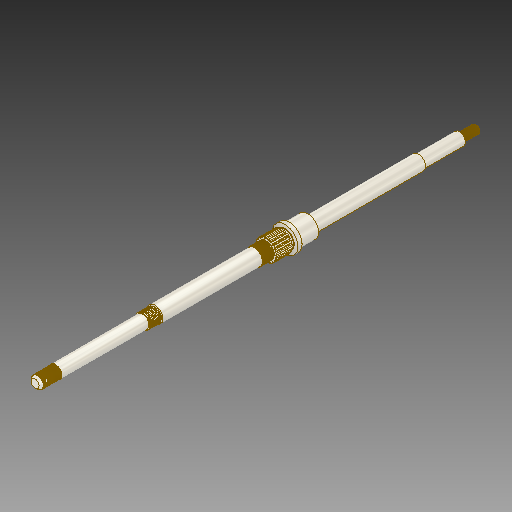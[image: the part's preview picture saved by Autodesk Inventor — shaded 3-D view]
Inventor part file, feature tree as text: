
AUTODESK INVENTOR PART (.ipt)
format: ipt  version: 2019 (Build 230136000, 136)  size: 991,232 bytes
history: native  units: mm
features: sketch x24, extrude x18, projected_geometry x7, helix x4, plane x3, split x2, fillet x2, hole x1, chamfer x1, other x1, revolve x1
ambient origin geometry x8: Origin, YZ Plane, XZ Plane, XY Plane, X Axis, Y Axis, Z Axis, Center Point
bodies: Solid1 (feature_tree)
feature tree (64):
  extrude  "Extrusion1"  Depth=23.0mm TaperAngle=0.0deg
  helix  "Coil1"  [1 undecoded]
  split  "Split1"
  extrude  "Extrusion2"  Depth=0.5mm
  extrude  "Extrusion16"  Depth=0.5mm
  extrude  "Extrusion3"  Depth=1.5mm
  extrude  "Extrusion4"  Depth=160.0mm TaperAngle=0.0deg
  extrude  "Extrusion5"  Depth=25.841mm TaperAngle=0.0deg
  extrude  "Extrusion6"  Depth=6.0mm TaperAngle=0.0deg
  extrude  "Extrusion7"  Depth=4.0mm TaperAngle=0.0deg
  extrude  "Extrusion8"  Depth=1.0mm
  extrude  "Extrusion9"  Depth=13.0mm
  helix  "Coil2"  [1 undecoded]
  extrude  "Extrusion10"  Depth=22.0mm TaperAngle=0.0deg
  plane  "Work Plane1"
  extrude  "Extrusion11"  Depth=155.0mm TaperAngle=0.0deg
  extrude  "Extrusion12"  TaperAngle=60.0deg  [1 undecoded]
  helix  "Coil3"  [1 undecoded]
  extrude  "Extrusion13"  Depth=0.5mm
  plane  "Work Plane2"
  extrude  "Extrusion14"  Depth=25.0mm
  extrude  "Extrusion15"  Depth=25.0mm
  helix  "Coil4"  [1 undecoded]
  split  "Split2"
  plane  "Work Plane3"
  hole  "Hole1"  [1 undecoded]
  fillet  "Fillet1"  Radius=1.241mm
  chamfer  "Chamfer1"  Distance=1.3mm
  fillet  "Fillet2"  [1 undecoded]
  extrude  "Extrusion17"  Depth=1.3mm TaperAngle=0.0deg
  extrude  "Extrusion18"  Depth=1.5mm TaperAngle=0.0deg
  sketch  "Sketch1"  dims[d0=10.5mm d1=23.0mm d2=0.0mm d7=0.747mm]
  sketch  "Sketch2"  dims[d9=60.0deg d10=0.5mm]
  sketch  "Sketch3"  dims[d12=60.0deg]
  sketch  "Sketch4"  dims[d14=1.0mm d15=0.5mm d16=230.0mm d17=0.0mm d18=90.0deg d19=90.0deg d20=0.0mm d21=0.0mm d22=12.0mm]
  sketch  "Sketch5"  dims[d23=1.5mm d24=0.0mm d25=20.0mm]
  sketch  "Sketch6"  dims[d26=154.0mm d27=0.0mm d29=160.0mm d30=0.0mm]
  sketch  "Sketch7"  dims[d31=30.0mm d32=25.841mm d33=0.0mm]
  sketch  "Sketch8"  dims[d34=36.0mm d35=6.0mm d36=0.0mm]
  sketch  "Sketch9"  dims[d37=25.0mm d38=4.0mm d39=0.0mm]
  sketch  "Sketch10"  dims[d40=29.0mm d41=1.0mm]
  sketch  "Sketch11"  dims[d42=13.0mm d43=19.896753mm d44=19.896753mm]
  projected_geometry  "Projected Loop2"
  sketch  "Sketch12"  dims[d45=220.0mm d47=360.0deg d49=22.0mm d50=0.0mm]
  sketch  "Sketch13"  dims[d51=22.0mm d52=155.0mm d53=0.0mm]
  projected_geometry  "Projected Loop3"
  sketch  "Sketch14"  dims[d54=0.717mm d56=60.0deg d57=0.45mm]
  sketch  "Sketch15"  dims[d58=1.0mm d59=0.5mm d60=230.0mm d61=0.0mm d62=90.0deg d63=90.0deg d64=0.0mm d65=0.0mm d66=21.4mm]
  projected_geometry  "Projected Loop4"
  sketch  "Sketch16"  dims[d67=1.7mm d68=0.0mm d69=25.0mm]
  sketch  "Sketch17"  dims[d70=-14.7mm d71=25.0mm d72=1.7mm d73=0.0mm]
  projected_geometry  "Projected Loop5"
  sketch  "Sketch18"  dims[d74=18.0mm d75=138.737mm d76=0.0mm d77=1.241mm]
  sketch  "Sketch19"  dims[d79=60.0deg]
  projected_geometry  "Projected Loop6"
  sketch  "Sketch20"  dims[d80=0.95mm]
  projected_geometry  "Projected Loop7"
  other  "Srf1"
  sketch  "Sketch21"  dims[d82=1.096966mm]
  sketch  "Sketch22"  dims[d83=1.5mm d84=10.0mm d85=200.0mm d86=0.0mm d87=90.0deg d88=90.0deg d89=0.0mm d90=0.0mm d91=1.3mm d92=0.0mm d93=-16.0mm]
  sketch  "Sketch23"  dims[d94=22.0mm d95=1.3mm d96=0.0mm]
  projected_geometry  "Projected Loop8"
  sketch  "Sketch24"  dims[d97=16.0mm d98=28.5mm d99=0.0mm d104=0.746mm d105=60.0deg d107=0.5mm d108=0.57735mm d109=1.0mm d110=10.0mm d111=300.0mm d112=0.0mm d113=90.0deg d114=90.0deg d115=0.0mm d116=0.0mm d117=6.859144mm d118=11.332mm d121=90.0deg d122=19.617501mm d123=8.25mm d124=3.5mm d125=6.0mm d126=4.0mm d127=2.0mm d128=90.0deg d129=8.0mm d130=20.594885mm d131=1.0mm d132=0.2mm d133=2.0mm d134=45.0deg d135=0.5mm d136=14.0mm d137=17.0mm d138=57.0mm d139=0.0mm d140=12.0mm d141=20.0mm d142=0.0mm d143=10.5mm d144=1.5mm d145=-7.853982mm]
  revolve  "RevolutionSrf1"  [1 undecoded]
note: 8 required parameter values undecoded (feature->parameter linkage not recoverable at this tier; creation-order binding heuristic only, values carry confidence <= 0.55)